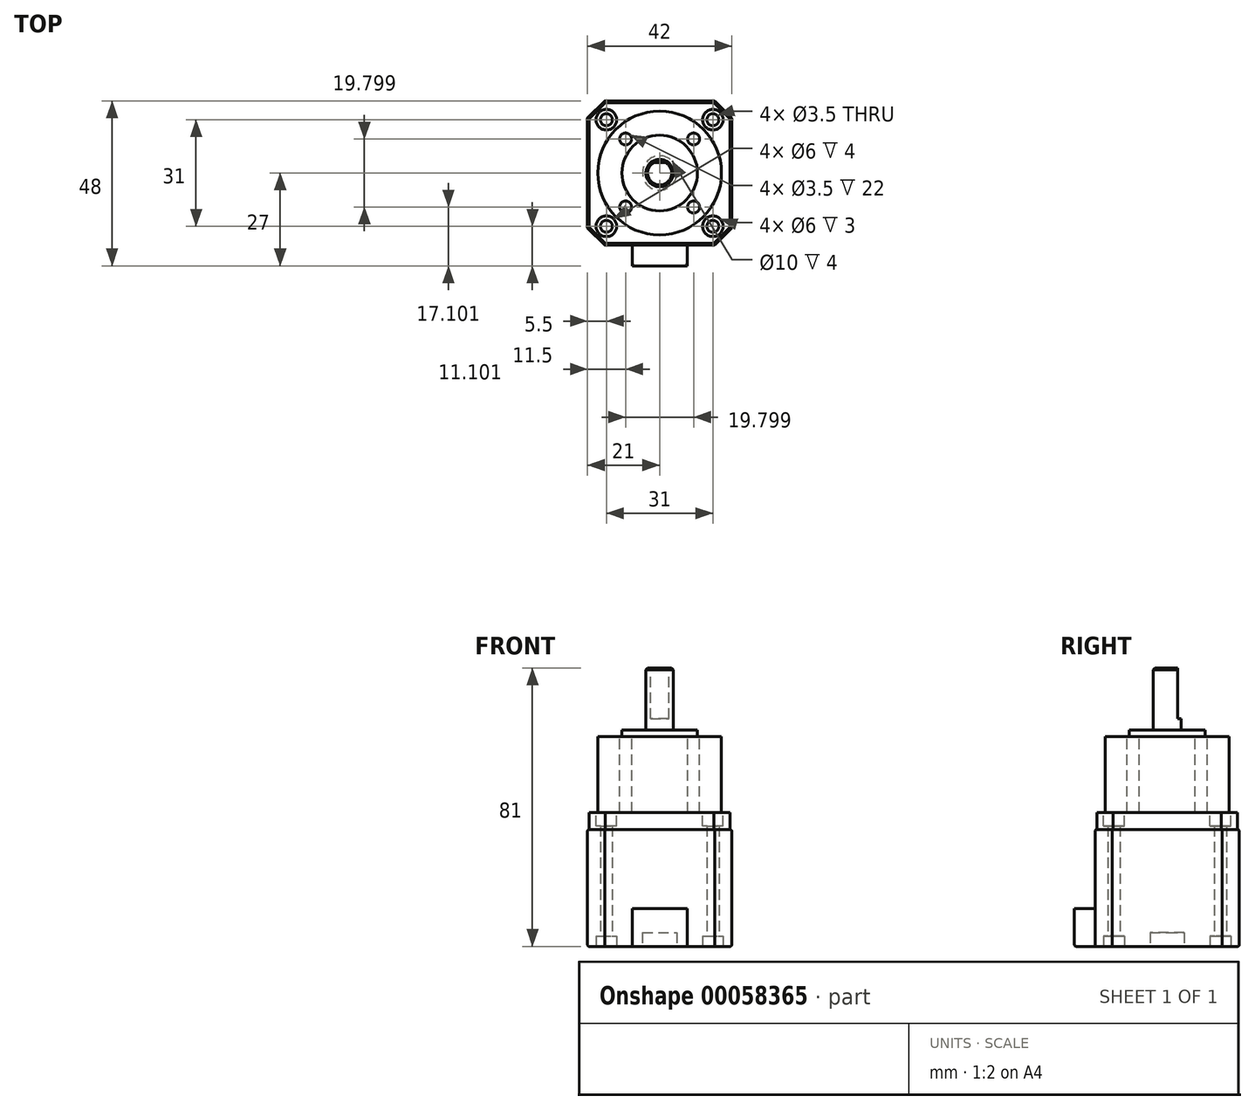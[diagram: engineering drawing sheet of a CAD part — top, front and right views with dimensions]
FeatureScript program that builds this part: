
annotation { "Feature Type Name" : "Feature", "Feature Type Description" : "" }
export const myFeature = defineFeature(function(context is Context, id is Id, definition is map)
    precondition{}
    {
        {
            var Q0;
            Q0=qCreatedBy(makeId("Top.planeOp"),FACE);
            var sketch = newSketch(context, id + "F0", { "sketchPlane" : qUnion([Q0])});
            skLineSegment(sketch, "E0.rect.bottom", {"start": v(21, 21) * mm, "end": v(-21, 21) * mm});
            skLineSegment(sketch, "E0.rect.top", {"start": v(21, -21) * mm, "end": v(-21, -21) * mm});
            skLineSegment(sketch, "E0.rect.left", {"start": v(21, 21) * mm, "end": v(21, -21) * mm});
            skLineSegment(sketch, "E0.rect.right", {"start": v(-21, 21) * mm, "end": v(-21, -21) * mm});
            skPoint(sketch, "E0.rect.middle", {"position": v(0, 0) * mm});
            skSolve(sketch);
        }
        {
            var Q0;
            Q0 = qSketchRegion(id + "F0", true);
            extrude(context, id + "F1", {"entities" : qUnion([Q0]), "depth" : 34 * mm});
        }
        {
            var Q0;
            Q0=makeQuery(id+"F1.opExtrude","SWEPT_EDGE",EDGE,{"disambiguationData":[OSD([sQuery(id+"F0.wireOp",EDGE,"E0.rect.top"),sQuery(id+"F0.wireOp",EDGE,"E0.rect.right")])]});
            var Q1;
            Q1=makeQuery(id+"F1.opExtrude","SWEPT_EDGE",EDGE,{"disambiguationData":[OSD([sQuery(id+"F0.wireOp",EDGE,"E0.rect.top"),sQuery(id+"F0.wireOp",EDGE,"E0.rect.left")])]});
            var Q2;
            Q2=makeQuery(id+"F1.opExtrude","SWEPT_EDGE",EDGE,{"disambiguationData":[OSD([sQuery(id+"F0.wireOp",EDGE,"E0.rect.bottom"),sQuery(id+"F0.wireOp",EDGE,"E0.rect.left")])]});
            var Q3;
            Q3=makeQuery(id+"F1.opExtrude","SWEPT_EDGE",EDGE,{"disambiguationData":[OSD([sQuery(id+"F0.wireOp",EDGE,"E0.rect.bottom"),sQuery(id+"F0.wireOp",EDGE,"E0.rect.right")])]});
            chamfer(context, id + "F2", {"entities" : qUnion([Q0, Q1, Q2, Q3]), "width" : 5 * mm, "tangentPropagation" : true});
        }
        {
            var Q0;
            Q0=qCreatedBy(makeId("Top.planeOp"),FACE);
            var sketch = newSketch(context, id + "F3", { "sketchPlane" : qUnion([Q0])});
            skLineSegment(sketch, "E1.rect.bottom", {"start": v(8, -21) * mm, "end": v(-8, -21) * mm});
            skLineSegment(sketch, "E1.rect.top", {"start": v(8, -27) * mm, "end": v(-8, -27) * mm});
            skLineSegment(sketch, "E1.rect.left", {"start": v(8, -21) * mm, "end": v(8, -27) * mm});
            skLineSegment(sketch, "E1.rect.right", {"start": v(-8, -21) * mm, "end": v(-8, -27) * mm});
            skPoint(sketch, "E1.rect.middle", {"position": v(0, -24) * mm});
            skSolve(sketch);
        }
        {
            var Q0;
            Q0 = qSketchRegion(id + "F3", true);
            extrude(context, id + "F4", {"entities" : qUnion([Q0]), "operationType" : NewBodyOperationType.ADD, "depth" : 11 * mm});
        }
        {
            var Q0;
            Q0=makeQuery(id+"F1.opExtrude","CAP_FACE",FACE,{"disambiguationData":[OSD([sQuery(id+"F0.wireOp",EDGE,"E0.rect.bottom"),sQuery(id+"F0.wireOp",EDGE,"E0.rect.top"),sQuery(id+"F0.wireOp",EDGE,"E0.rect.left"),sQuery(id+"F0.wireOp",EDGE,"E0.rect.right")])],"isStart":false});
            var Q1;
            Q1=makeQuery(id+"F4.boolean.opBoolean","MERGE",FACE,{"derivedFrom":[makeQuery(id+"F1.opExtrude","CAP_FACE",FACE,{"disambiguationData":[OSD([sQuery(id+"F0.wireOp",EDGE,"E0.rect.bottom"),sQuery(id+"F0.wireOp",EDGE,"E0.rect.top"),sQuery(id+"F0.wireOp",EDGE,"E0.rect.left"),sQuery(id+"F0.wireOp",EDGE,"E0.rect.right")])],"isStart":true}),makeQuery(id+"F4.opExtrude","CAP_FACE",FACE,{"disambiguationData":[OSD([sQuery(id+"F3.wireOp",EDGE,"E1.rect.bottom"),sQuery(id+"F3.wireOp",EDGE,"E1.rect.top"),sQuery(id+"F3.wireOp",EDGE,"E1.rect.left"),sQuery(id+"F3.wireOp",EDGE,"E1.rect.right")])],"isStart":true})]});
            fillet(context, id + "F5", {"entities" : qUnion([Q0, Q1]), "radius" : 0.5 * mm, "tangentPropagation" : true, "allowEdgeOverflow" : false});
        }
        {
            var Q0;
            Q0=makeQuery(id+"F1.opExtrude","CAP_FACE",FACE,{"disambiguationData":[OSD([sQuery(id+"F0.wireOp",EDGE,"E0.rect.bottom"),sQuery(id+"F0.wireOp",EDGE,"E0.rect.top"),sQuery(id+"F0.wireOp",EDGE,"E0.rect.left"),sQuery(id+"F0.wireOp",EDGE,"E0.rect.right")])],"isStart":false});
            extrude(context, id + "F6", {"entities" : qUnion([Q0]), "operationType" : NewBodyOperationType.ADD, "depth" : 5 * mm});
        }
        {
            var Q0;
            Q0=makeQuery(id+"F4.boolean.opBoolean","MERGE",FACE,{"derivedFrom":[makeQuery(id+"F1.opExtrude","CAP_FACE",FACE,{"disambiguationData":[OSD([sQuery(id+"F0.wireOp",EDGE,"E0.rect.bottom"),sQuery(id+"F0.wireOp",EDGE,"E0.rect.top"),sQuery(id+"F0.wireOp",EDGE,"E0.rect.left"),sQuery(id+"F0.wireOp",EDGE,"E0.rect.right")])],"isStart":true}),makeQuery(id+"F4.opExtrude","CAP_FACE",FACE,{"disambiguationData":[OSD([sQuery(id+"F3.wireOp",EDGE,"E1.rect.bottom"),sQuery(id+"F3.wireOp",EDGE,"E1.rect.top"),sQuery(id+"F3.wireOp",EDGE,"E1.rect.left"),sQuery(id+"F3.wireOp",EDGE,"E1.rect.right")])],"isStart":true})]});
            var sketch = newSketch(context, id + "F7", { "sketchPlane" : qUnion([Q0])});
            skCircle(sketch, "E2", {"center": v(-15.5, 15.5) * mm, "radius": 1.75 * mm});
            skCircle(sketch, "E3", {"center": v(0, 0) * mm, "radius": 21.92 * mm, "construction": true});
            skCircle(sketch, "E4.1.0", {"center": v(-15.5, -15.5) * mm, "radius": 1.75 * mm});
            skCircle(sketch, "E4.2.0", {"center": v(15.5, -15.5) * mm, "radius": 1.75 * mm});
            skCircle(sketch, "E4.3.0", {"center": v(15.5, 15.5) * mm, "radius": 1.75 * mm});
            skSolve(sketch);
        }
        {
            var Q0;
            Q0 = qSketchRegion(id + "F7", true);
            extrude(context, id + "F8", {"entities" : qUnion([Q0]), "operationType" : NewBodyOperationType.REMOVE, "endBound" : BoundingType.THROUGH_ALL, "oppositeDirection" : true, "depth" : 25 * mm});
        }
        {
            var Q0;
            Q0=makeQuery(id+"F6.opExtrude","CAP_FACE",FACE,{"disambiguationData":[OSD([sQuery(id+"F0.wireOp",EDGE,"E0.rect.bottom"),sQuery(id+"F0.wireOp",EDGE,"E0.rect.top"),sQuery(id+"F0.wireOp",EDGE,"E0.rect.left"),sQuery(id+"F0.wireOp",EDGE,"E0.rect.right")])],"isStart":false});
            var sketch = newSketch(context, id + "F9", { "sketchPlane" : qUnion([Q0])});
            skCircle(sketch, "E5", {"center": v(-15.5, 15.5) * mm, "radius": 3 * mm});
            skCircle(sketch, "E6.1.0", {"center": v(-15.5, -15.5) * mm, "radius": 3 * mm});
            skCircle(sketch, "E6.2.0", {"center": v(15.5, -15.5) * mm, "radius": 3 * mm});
            skCircle(sketch, "E6.3.0", {"center": v(15.5, 15.5) * mm, "radius": 3 * mm});
            skPoint(sketch, "E6.center", {"position": v(0, 0) * mm});
            skSolve(sketch);
        }
        {
            var Q0;
            Q0 = qSketchRegion(id + "F9", true);
            extrude(context, id + "F10", {"entities" : qUnion([Q0]), "operationType" : NewBodyOperationType.REMOVE, "oppositeDirection" : true, "depth" : 4 * mm});
        }
        {
            var Q0;
            Q0=makeQuery(id+"F6.opExtrude","CAP_FACE",FACE,{"disambiguationData":[OSD([sQuery(id+"F0.wireOp",EDGE,"E0.rect.bottom"),sQuery(id+"F0.wireOp",EDGE,"E0.rect.top"),sQuery(id+"F0.wireOp",EDGE,"E0.rect.left"),sQuery(id+"F0.wireOp",EDGE,"E0.rect.right")])],"isStart":false});
            var sketch = newSketch(context, id + "F11", { "sketchPlane" : qUnion([Q0])});
            skCircle(sketch, "E7", {"center": v(0, 0) * mm, "radius": 18 * mm});
            skSolve(sketch);
        }
        {
            var Q0;
            Q0 = qSketchRegion(id + "F11", true);
            extrude(context, id + "F12", {"entities" : qUnion([Q0]), "operationType" : NewBodyOperationType.ADD, "depth" : 22 * mm});
        }
        {
            var Q0;
            Q0=makeQuery(id+"F12.opExtrude","CAP_FACE",FACE,{"disambiguationData":[OSD([sQuery(id+"F11.wireOp",EDGE,"E7")])],"isStart":false});
            var sketch = newSketch(context, id + "F13", { "sketchPlane" : qUnion([Q0])});
            skCircle(sketch, "E8", {"center": v(0, 0) * mm, "radius": 11 * mm});
            skSolve(sketch);
        }
        {
            var Q0;
            Q0 = qSketchRegion(id + "F13", true);
            extrude(context, id + "F14", {"entities" : qUnion([Q0]), "operationType" : NewBodyOperationType.ADD, "depth" : 2 * mm});
        }
        {
            var Q0;
            Q0=makeQuery(id+"F12.opExtrude","CAP_FACE",FACE,{"disambiguationData":[OSD([sQuery(id+"F11.wireOp",EDGE,"E7")])],"isStart":false});
            var sketch = newSketch(context, id + "F15", { "sketchPlane" : qUnion([Q0])});
            skCircle(sketch, "E9", {"center": v(0, 0) * mm, "radius": 4 * mm});
            skSolve(sketch);
        }
        {
            var Q0;
            Q0 = qSketchRegion(id + "F15", true);
            extrude(context, id + "F16", {"entities" : qUnion([Q0]), "operationType" : NewBodyOperationType.ADD, "depth" : 20 * mm});
        }
        {
            var Q0;
            Q0=makeQuery(id+"F16.opExtrude","CAP_EDGE",EDGE,{"disambiguationData":[OSD([sQuery(id+"F15.wireOp",EDGE,"E9")])],"isStart":false});
            chamfer(context, id + "F17", {"entities" : qUnion([Q0]), "width" : 0.5 * mm, "tangentPropagation" : true});
        }
        {
            var Q0;
            Q0=makeQuery(id+"F16.opExtrude","CAP_FACE",FACE,{"disambiguationData":[OSD([sQuery(id+"F15.wireOp",EDGE,"E9")])],"isStart":false});
            var sketch = newSketch(context, id + "F18", { "sketchPlane" : qUnion([Q0])});
            skArc(sketch, "E10", {"start": v(2.65, 3) * mm, "mid": v(0, 4) * mm, "end": v(-2.65, 3) * mm});
            skLineSegment(sketch, "E11", {"start": v(-2.65, 3) * mm, "end": v(2.65, 3) * mm});
            skSolve(sketch);
        }
        {
            var Q0;
            Q0 = qSketchRegion(id + "F18", true);
            extrude(context, id + "F19", {"entities" : qUnion([Q0]), "operationType" : NewBodyOperationType.REMOVE, "oppositeDirection" : true, "depth" : 14.75 * mm});
        }
        {
            var Q0;
            Q0=makeQuery(id+"F12.opExtrude","CAP_FACE",FACE,{"disambiguationData":[OSD([sQuery(id+"F11.wireOp",EDGE,"E7")])],"isStart":false});
            var sketch = newSketch(context, id + "F20", { "sketchPlane" : qUnion([Q0])});
            skCircle(sketch, "E12", {"center": v(-9.9, 9.9) * mm, "radius": 1.75 * mm});
            skCircle(sketch, "E13.1.0", {"center": v(-9.9, -9.9) * mm, "radius": 1.75 * mm});
            skCircle(sketch, "E13.2.0", {"center": v(9.9, -9.9) * mm, "radius": 1.75 * mm});
            skCircle(sketch, "E13.3.0", {"center": v(9.9, 9.9) * mm, "radius": 1.75 * mm});
            skPoint(sketch, "E13.center", {"position": v(0, 0) * mm});
            skCircle(sketch, "E14", {"center": v(0, 0) * mm, "radius": 14 * mm, "construction": true});
            skSolve(sketch);
        }
        {
            var Q0;
            Q0 = qSketchRegion(id + "F20", true);
            var Q1;
            Q1=makeQuery(id+"F6.opExtrude","CAP_FACE",FACE,{"disambiguationData":[OSD([sQuery(id+"F0.wireOp",EDGE,"E0.rect.bottom"),sQuery(id+"F0.wireOp",EDGE,"E0.rect.top"),sQuery(id+"F0.wireOp",EDGE,"E0.rect.left"),sQuery(id+"F0.wireOp",EDGE,"E0.rect.right")])],"isStart":false});
            extrude(context, id + "F21", {"entities" : qUnion([Q0]), "operationType" : NewBodyOperationType.REMOVE, "endBound" : BoundingType.UP_TO_SURFACE, "oppositeDirection" : true, "endBoundEntityFace" : qUnion([Q1]), "depth" : 25 * mm});
        }
        {
            var Q0;
            Q0=makeQuery(id+"F4.boolean.opBoolean","MERGE",FACE,{"derivedFrom":[makeQuery(id+"F1.opExtrude","CAP_FACE",FACE,{"disambiguationData":[OSD([sQuery(id+"F0.wireOp",EDGE,"E0.rect.bottom"),sQuery(id+"F0.wireOp",EDGE,"E0.rect.top"),sQuery(id+"F0.wireOp",EDGE,"E0.rect.left"),sQuery(id+"F0.wireOp",EDGE,"E0.rect.right")])],"isStart":true}),makeQuery(id+"F4.opExtrude","CAP_FACE",FACE,{"disambiguationData":[OSD([sQuery(id+"F3.wireOp",EDGE,"E1.rect.bottom"),sQuery(id+"F3.wireOp",EDGE,"E1.rect.top"),sQuery(id+"F3.wireOp",EDGE,"E1.rect.left"),sQuery(id+"F3.wireOp",EDGE,"E1.rect.right")])],"isStart":true})]});
            var sketch = newSketch(context, id + "F22", { "sketchPlane" : qUnion([Q0])});
            skCircle(sketch, "E15", {"center": v(-15.5, 15.5) * mm, "radius": 3 * mm});
            skCircle(sketch, "E16.1.0", {"center": v(-15.5, -15.5) * mm, "radius": 3 * mm});
            skCircle(sketch, "E16.2.0", {"center": v(15.5, -15.5) * mm, "radius": 3 * mm});
            skCircle(sketch, "E16.3.0", {"center": v(15.5, 15.5) * mm, "radius": 3 * mm});
            skPoint(sketch, "E16.center", {"position": v(0, 0) * mm});
            skSolve(sketch);
        }
        {
            var Q0;
            Q0 = qSketchRegion(id + "F22", true);
            extrude(context, id + "F23", {"entities" : qUnion([Q0]), "operationType" : NewBodyOperationType.REMOVE, "oppositeDirection" : true, "depth" : 3 * mm});
        }
        {
            var Q0;
            Q0=makeQuery(id+"F4.boolean.opBoolean","MERGE",FACE,{"derivedFrom":[makeQuery(id+"F1.opExtrude","CAP_FACE",FACE,{"disambiguationData":[OSD([sQuery(id+"F0.wireOp",EDGE,"E0.rect.bottom"),sQuery(id+"F0.wireOp",EDGE,"E0.rect.top"),sQuery(id+"F0.wireOp",EDGE,"E0.rect.left"),sQuery(id+"F0.wireOp",EDGE,"E0.rect.right")])],"isStart":true}),makeQuery(id+"F4.opExtrude","CAP_FACE",FACE,{"disambiguationData":[OSD([sQuery(id+"F3.wireOp",EDGE,"E1.rect.bottom"),sQuery(id+"F3.wireOp",EDGE,"E1.rect.top"),sQuery(id+"F3.wireOp",EDGE,"E1.rect.left"),sQuery(id+"F3.wireOp",EDGE,"E1.rect.right")])],"isStart":true})]});
            var sketch = newSketch(context, id + "F24", { "sketchPlane" : qUnion([Q0])});
            skCircle(sketch, "E17", {"center": v(0, 0) * mm, "radius": 5 * mm});
            skSolve(sketch);
        }
        {
            var Q0;
            Q0 = qSketchRegion(id + "F24", true);
            extrude(context, id + "F25", {"entities" : qUnion([Q0]), "operationType" : NewBodyOperationType.REMOVE, "oppositeDirection" : true, "depth" : 4 * mm});
        }
    });
